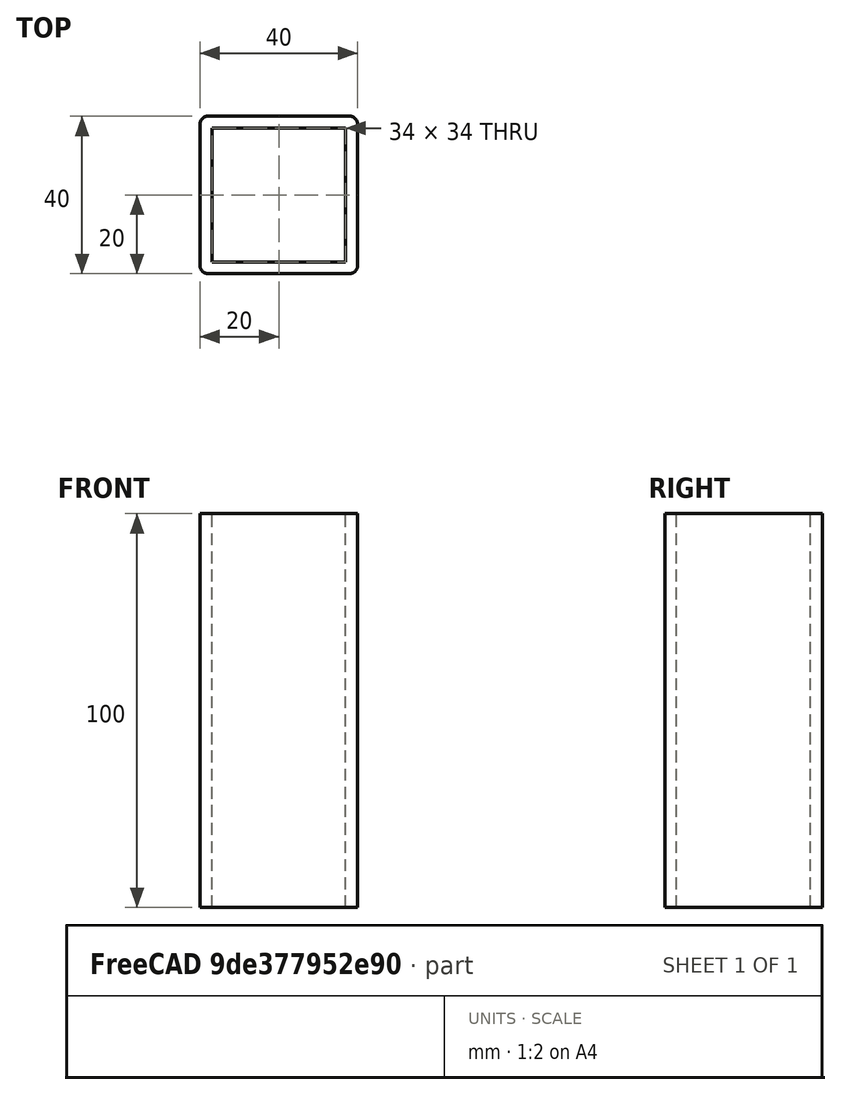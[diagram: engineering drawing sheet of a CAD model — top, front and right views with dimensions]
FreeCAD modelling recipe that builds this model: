
FCSTD DOCUMENT  (FreeCAD 1.0R39319 (Git))
Label: steel-profile-40x40x100
License: All rights reserved
LicenseURL: http://en.wikipedia.org/wiki/All_rights_reserved
objects: Sketcher::SketchObject×1, PartDesign::Pad×1, PartDesign::Body×1, App::Part×1
note: 6 computed .brp shape members not serialized (recipe doc carries the construction recipe); baked Part::Feature solids carry a one-line shape summary decoded from their .brp

FEATURE [Sketcher::SketchObject] Sketch
  ArcFitTolerance = 1e-06
  AttachmentSupport = -> [XY_Plane001]
  FullyConstrained = true
  MakeInternals = false
  MapMode = 5
  sketch-geometry (18):
    g0: LineSegment StartX=2 StartY=0 StartZ=0 EndX=38 EndY=0 EndZ=0
    g1: LineSegment StartX=40 StartY=2 StartZ=0 EndX=40 EndY=38 EndZ=0
    g2: LineSegment StartX=38 StartY=40 StartZ=0 EndX=2 EndY=40 EndZ=0
    g3: LineSegment StartX=0 StartY=38 StartZ=0 EndX=0 EndY=2 EndZ=0
    g4: ArcOfCircle CenterX=2 CenterY=2 CenterZ=0 NormalX=0 NormalY=0 NormalZ=1 AngleXU=0 Radius=2 StartAngle=3.14159 EndAngle=4.71239
    g5: ArcOfCircle CenterX=38 CenterY=2 CenterZ=0 NormalX=0 NormalY=0 NormalZ=1 AngleXU=0 Radius=2 StartAngle=4.71239 EndAngle=6.28319
    g6: ArcOfCircle CenterX=38 CenterY=38 CenterZ=0 NormalX=0 NormalY=0 NormalZ=1 AngleXU=0 Radius=2 StartAngle=0 EndAngle=1.5708
    g7: ArcOfCircle CenterX=2 CenterY=38 CenterZ=0 NormalX=0 NormalY=0 NormalZ=1 AngleXU=0 Radius=2 StartAngle=1.5708 EndAngle=3.14159
    g8: LineSegment StartX=3 StartY=3 StartZ=0 EndX=37 EndY=3 EndZ=0
    g9: LineSegment StartX=37 StartY=3 StartZ=0 EndX=37 EndY=37 EndZ=0
    g10: LineSegment StartX=37 StartY=37 StartZ=0 EndX=3 EndY=37 EndZ=0
    g11: LineSegment StartX=3 StartY=37 StartZ=0 EndX=3 EndY=3 EndZ=0
    g12: LineSegment [constr] StartX=2 StartY=2 StartZ=0 EndX=3 EndY=3 EndZ=0
    g13: LineSegment [constr] StartX=38 StartY=2 StartZ=0 EndX=37 EndY=3 EndZ=0
    g14: LineSegment [constr] StartX=38 StartY=38 StartZ=0 EndX=37 EndY=37 EndZ=0
    g15: LineSegment [constr] StartX=2 StartY=38 StartZ=0 EndX=3 EndY=37 EndZ=0
    g16: GeomPoint [constr] X=0 Y=0 Z=0
    g17: GeomPoint [constr] X=40 Y=40 Z=0
  constraints (43):
    c: Tangent(g0,g4) = -1.5708
    c: Tangent(g0,g5) = -1.5708
    c: Tangent(g1,g5) = -1.5708
    c: Tangent(g1,g6) = -1.5708
    c: Tangent(g2,g6) = -1.5708
    c: Tangent(g2,g7) = -1.5708
    c: Tangent(g3,g7) = -1.5708
    c: Tangent(g3,g4) = -1.5708
    c: Horizontal(g0)
    c: Horizontal(g2)
    c: Vertical(g1)
    c: Vertical(g3)
    c: Equal(g4,g5)
    c: Equal(g5,g6)
    c: Equal(g6,g7)
    c: Coincident(g8,g9)
    c: Coincident(g9,g10)
    c: Coincident(g10,g11)
    c: Coincident(g11,g8)
    c: Horizontal(g8)
    c: Horizontal(g10)
    c: Vertical(g9)
    c: Vertical(g11)
    c: Coincident(g12,g4)
    c: Coincident(g12,g8)
    c: Coincident(g13,g5)
    c: Coincident(g13,g9)
    c: Coincident(g14,g6)
    c: Coincident(g14,g10)
    c: Coincident(g15,g7)
    c: Coincident(g15,g11)
    c: Perpendicular(g12,g13)
    c: Perpendicular(g13,g14)
    c: Perpendicular(g14,g15)
    c: PointOnObject(g16,g0)
    c: PointOnObject(g16,g3)
    c: PointOnObject(g17,g1)
    c: PointOnObject(g17,g2)
    c: Distance(g1,g3) = 40
    c: Distance(g0,g2) = 40
    c: Radius(g5) = 2
    c: Distance(g8,g0) = 3
    c: Coincident(g16,g-1)
FEATURE [PartDesign::Pad] Pad
  Direction = (0,0,1)
  Length = 100
  Length2 = 10
  Profile = -> Sketch
  ReferenceAxis = -> Sketch [N_Axis]
  Suppressed = false
  Type = 0
FEATURE [PartDesign::Body] Body
  AllowCompound = false
  Group = -> [Sketch,Pad]
  Origin = -> Origin001
  Tip = -> Pad
FEATURE [App::Part] Part  label="40x40x100mm-profile"
  Group = -> [Body]
  Origin = -> Origin
